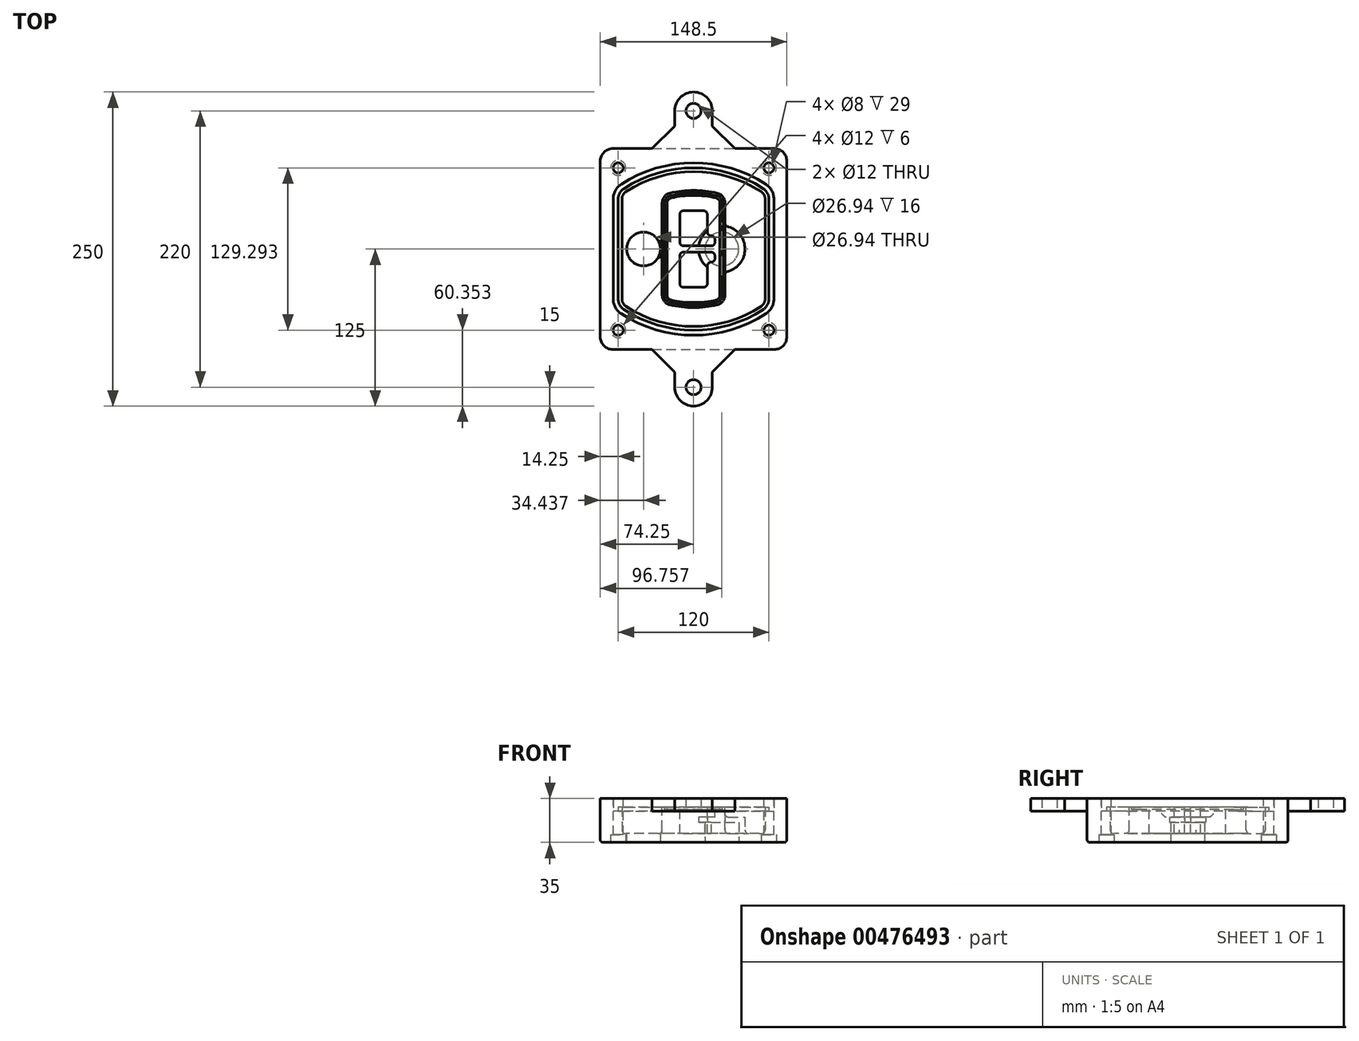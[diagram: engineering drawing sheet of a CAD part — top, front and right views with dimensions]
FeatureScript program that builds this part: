
annotation { "Feature Type Name" : "Feature", "Feature Type Description" : "" }
export const myFeature = defineFeature(function(context is Context, id is Id, definition is map)
    precondition{}
    {
        {
            var Q0;
            Q0=qCreatedBy(makeId("Top.planeOp"),FACE);
            var sketch = newSketch(context, id + "F0", { "sketchPlane" : qUnion([Q0])});
            skPoint(sketch, "E0.rect.middle", {"position": v(0, 0) * mm});
            skLineSegment(sketch, "E1.bottom", {"start": v(-64.25, -80) * mm, "end": v(64.25, -80) * mm});
            skLineSegment(sketch, "E1.top", {"start": v(-64.25, 80) * mm, "end": v(64.25, 80) * mm});
            skLineSegment(sketch, "E1.left", {"start": v(-74.25, -70) * mm, "end": v(-74.25, 70) * mm});
            skLineSegment(sketch, "E1.right", {"start": v(74.25, -70) * mm, "end": v(74.25, 70) * mm});
            skLineSegment(sketch, "E2", {"start": v(-74.25, 80) * mm, "end": v(74.25, -80) * mm, "construction": true});
            skLineSegment(sketch, "E3", {"start": v(74.25, 80) * mm, "end": v(-74.25, -80) * mm, "construction": true});
            skCircle(sketch, "E4", {"center": v(-60, 64.65) * mm, "radius": 4 * mm});
            skCircle(sketch, "E5", {"center": v(60, 64.65) * mm, "radius": 4 * mm});
            skCircle(sketch, "E6", {"center": v(60, -64.65) * mm, "radius": 4 * mm});
            skCircle(sketch, "E7", {"center": v(-60, -64.65) * mm, "radius": 4 * mm});
            skLineSegment(sketch, "E8", {"start": v(-60, 64.65) * mm, "end": v(60, 64.65) * mm, "construction": true});
            skLineSegment(sketch, "E9", {"start": v(60, 64.65) * mm, "end": v(60, -64.65) * mm, "construction": true});
            skLineSegment(sketch, "E10", {"start": v(60, -64.65) * mm, "end": v(-60, -64.65) * mm, "construction": true});
            skLineSegment(sketch, "E11", {"start": v(-60, -64.65) * mm, "end": v(-60, 64.65) * mm, "construction": true});
            skLineSegment(sketch, "E12", {"start": v(-60, 39.77) * mm, "end": v(-60, -39.77) * mm});
            skLineSegment(sketch, "E13", {"start": v(60, 39.77) * mm, "end": v(60, -39.77) * mm});
            skArc(sketch, "E14", {"start": v(55.47, 48.14) * mm, "mid": v(0, 64.65) * mm, "end": v(-55.47, 48.14) * mm});
            skArc(sketch, "E15", {"start": v(-55.47, -48.14) * mm, "mid": v(0, -64.65) * mm, "end": v(55.47, -48.14) * mm});
            skLineSegment(sketch, "E16", {"start": v(-60, 0) * mm, "end": v(60, 0) * mm, "construction": true});
            skPoint(sketch, "E17.visualSharp", {"position": v(-60, -45) * mm});
            skArc(sketch, "E17.filletArc", {"start": v(-60, -39.77) * mm, "mid": v(-58.8, -44.53) * mm, "end": v(-55.47, -48.14) * mm});
            skPoint(sketch, "E18.visualSharp", {"position": v(-60, 45) * mm});
            skArc(sketch, "E18.filletArc", {"start": v(-55.47, 48.14) * mm, "mid": v(-58.8, 44.53) * mm, "end": v(-60, 39.77) * mm});
            skPoint(sketch, "E19.visualSharp", {"position": v(60, 45) * mm});
            skArc(sketch, "E19.filletArc", {"start": v(60, 39.77) * mm, "mid": v(58.8, 44.53) * mm, "end": v(55.47, 48.14) * mm});
            skPoint(sketch, "E20.visualSharp", {"position": v(60, -45) * mm});
            skArc(sketch, "E20.filletArc", {"start": v(55.47, -48.14) * mm, "mid": v(58.8, -44.53) * mm, "end": v(60, -39.77) * mm});
            skPoint(sketch, "E21.visualSharp", {"position": v(-74.25, 80) * mm});
            skArc(sketch, "E21.filletArc", {"start": v(-64.25, 80) * mm, "mid": v(-71.32, 77.07) * mm, "end": v(-74.25, 70) * mm});
            skPoint(sketch, "E22.visualSharp", {"position": v(74.25, 80) * mm});
            skArc(sketch, "E22.filletArc", {"start": v(74.25, 70) * mm, "mid": v(71.32, 77.07) * mm, "end": v(64.25, 80) * mm});
            skPoint(sketch, "E23.visualSharp", {"position": v(74.25, -80) * mm});
            skArc(sketch, "E23.filletArc", {"start": v(64.25, -80) * mm, "mid": v(71.32, -77.07) * mm, "end": v(74.25, -70) * mm});
            skPoint(sketch, "E24.visualSharp", {"position": v(-74.25, -80) * mm});
            skArc(sketch, "E24.filletArc", {"start": v(-74.25, -70) * mm, "mid": v(-71.32, -77.07) * mm, "end": v(-64.25, -80) * mm});
            skArc(sketch, "E25.0", {"start": v(57, 39.77) * mm, "mid": v(56.16, 43.1) * mm, "end": v(53.83, 45.63) * mm});
            skLineSegment(sketch, "E25.1", {"start": v(57, 39.77) * mm, "end": v(57, -39.77) * mm});
            skArc(sketch, "E25.2", {"start": v(53.83, -45.63) * mm, "mid": v(56.16, -43.1) * mm, "end": v(57, -39.77) * mm});
            skArc(sketch, "E25.3", {"start": v(-53.83, -45.63) * mm, "mid": v(0, -61.65) * mm, "end": v(53.83, -45.63) * mm});
            skArc(sketch, "E25.4", {"start": v(-57, -39.77) * mm, "mid": v(-56.16, -43.1) * mm, "end": v(-53.83, -45.63) * mm});
            skArc(sketch, "E25.5", {"start": v(53.83, 45.63) * mm, "mid": v(0, 61.65) * mm, "end": v(-53.83, 45.63) * mm});
            skLineSegment(sketch, "E25.6", {"start": v(-57, 39.77) * mm, "end": v(-57, -39.77) * mm});
            skArc(sketch, "E25.7", {"start": v(-53.83, 45.63) * mm, "mid": v(-56.16, 43.1) * mm, "end": v(-57, 39.77) * mm});
            skArc(sketch, "E26.0", {"start": v(-57.66, 51.49) * mm, "mid": v(-62.31, 46.43) * mm, "end": v(-64, 39.77) * mm});
            skArc(sketch, "E26.1", {"start": v(57.66, 51.49) * mm, "mid": v(0, 68.65) * mm, "end": v(-57.66, 51.49) * mm});
            skArc(sketch, "E26.2", {"start": v(64, 39.77) * mm, "mid": v(62.31, 46.43) * mm, "end": v(57.66, 51.49) * mm});
            skLineSegment(sketch, "E26.3", {"start": v(64, 39.77) * mm, "end": v(64, -39.77) * mm});
            skArc(sketch, "E26.4", {"start": v(57.66, -51.49) * mm, "mid": v(62.31, -46.43) * mm, "end": v(64, -39.77) * mm});
            skLineSegment(sketch, "E26.5", {"start": v(-64, 39.77) * mm, "end": v(-64, -39.77) * mm});
            skArc(sketch, "E26.6", {"start": v(-57.66, -51.49) * mm, "mid": v(0, -68.65) * mm, "end": v(57.66, -51.49) * mm});
            skArc(sketch, "E26.7", {"start": v(-64, -39.77) * mm, "mid": v(-62.31, -46.43) * mm, "end": v(-57.66, -51.49) * mm});
            skPoint(sketch, "E27.startSnap0", {"position": v(0, 68.65) * mm});
            skPoint(sketch, "E27.endSnap0", {"position": v(0, 64.65) * mm});
            skLineSegment(sketch, "E28", {"start": v(0, 110) * mm, "end": v(0, 80) * mm, "construction": true});
            skCircle(sketch, "E29", {"center": v(0, 110) * mm, "radius": 6 * mm});
            skArc(sketch, "E30", {"start": v(15, 110) * mm, "mid": v(0, 125) * mm, "end": v(-15, 110) * mm});
            skLineSegment(sketch, "E31", {"start": v(-15, 110) * mm, "end": v(-15, 98) * mm});
            skLineSegment(sketch, "E32", {"start": v(-15, 98) * mm, "end": v(-33, 80) * mm});
            skLineSegment(sketch, "E33", {"start": v(15, 110) * mm, "end": v(15, 98) * mm});
            skLineSegment(sketch, "E34", {"start": v(15, 98) * mm, "end": v(33, 80) * mm});
            skLineSegment(sketch, "E35.MirrorCS", {"start": v(15, -110) * mm, "end": v(15, -98) * mm});
            skLineSegment(sketch, "E36.MirrorCS", {"start": v(-15, -110) * mm, "end": v(-15, -98) * mm});
            skLineSegment(sketch, "E37.MirrorCS", {"start": v(0, -110) * mm, "end": v(0, -80) * mm, "construction": true});
            skLineSegment(sketch, "E38.MirrorCS", {"start": v(-15, -98) * mm, "end": v(-33, -80) * mm});
            skPoint(sketch, "E39.MirrorP", {"position": v(0, -68.65) * mm});
            skArc(sketch, "E40.MirrorCS", {"start": v(15, -110) * mm, "mid": v(0, -125) * mm, "end": v(-15, -110) * mm});
            skLineSegment(sketch, "E41.MirrorCS", {"start": v(15, -98) * mm, "end": v(33, -80) * mm});
            skCircle(sketch, "E42.MirrorC", {"center": v(0, -110) * mm, "radius": 6 * mm});
            skSolve(sketch);
        }
        {
            var Q0;
            Q0=makeQuery(id+"F0.imprint","IMPRINT",FACE,{"disambiguationData":[TD([[makeQuery(id+"F0.imprint","IMPRINT",EDGE,{"derivedFrom":sQuery(id+"F0.wireOp",EDGE,"E1.bottom")}),1.0]])]});
            var Q1;
            Q1=makeQuery(id+"F0.imprint","IMPRINT",FACE,{"disambiguationData":[TD([[makeQuery(id+"F0.imprint","IMPRINT",EDGE,{"derivedFrom":sQuery(id+"F0.wireOp",EDGE,"E12")}),1.0]])]});
            var Q2;
            Q2=makeQuery(id+"F0.imprint","IMPRINT",FACE,{"disambiguationData":[TD([[makeQuery(id+"F0.imprint","IMPRINT",EDGE,{"derivedFrom":sQuery(id+"F0.wireOp",EDGE,"E25.0")}),1.0]])]});
            var Q3;
            Q3=makeQuery(id+"F0.imprint","IMPRINT",FACE,{"disambiguationData":[TD([[makeQuery(id+"F0.imprint","IMPRINT",EDGE,{"derivedFrom":sQuery(id+"F0.wireOp",EDGE,"E12")}),-1.0]])]});
            extrude(context, id + "F1", {"entities" : qUnion([Q0, Q1, Q2, Q3]), "oppositeDirection" : true, "depth" : 25 * mm});
        }
        {
            var Q0;
            Q0=makeQuery(id+"F0.imprint","IMPRINT",FACE,{"disambiguationData":[TD([[makeQuery(id+"F0.imprint","IMPRINT",EDGE,{"derivedFrom":sQuery(id+"F0.wireOp",EDGE,"E12")}),1.0]])]});
            extrude(context, id + "F2", {"entities" : qUnion([Q0]), "operationType" : NewBodyOperationType.ADD, "depth" : 3 * mm});
        }
        {
            var Q0;
            Q0=makeQuery(id+"F0.imprint","IMPRINT",FACE,{"disambiguationData":[TD([[makeQuery(id+"F0.imprint","IMPRINT",EDGE,{"derivedFrom":sQuery(id+"F0.wireOp",EDGE,"E25.0")}),1.0]])]});
            extrude(context, id + "F3", {"entities" : qUnion([Q0]), "operationType" : NewBodyOperationType.REMOVE, "oppositeDirection" : true, "depth" : 18 * mm});
        }
        {
            var Q0;
            Q0=makeQuery(id+"F2.opExtrude","CAP_FACE",FACE,{"disambiguationData":[OSD([sQuery(id+"F0.wireOp",EDGE,"E12"),sQuery(id+"F0.wireOp",EDGE,"E13"),sQuery(id+"F0.wireOp",EDGE,"E14"),sQuery(id+"F0.wireOp",EDGE,"E15"),sQuery(id+"F0.wireOp",EDGE,"E17.filletArc"),sQuery(id+"F0.wireOp",EDGE,"E18.filletArc"),sQuery(id+"F0.wireOp",EDGE,"E19.filletArc"),sQuery(id+"F0.wireOp",EDGE,"E20.filletArc"),sQuery(id+"F0.wireOp",EDGE,"E25.0"),sQuery(id+"F0.wireOp",EDGE,"E25.1"),sQuery(id+"F0.wireOp",EDGE,"E25.2"),sQuery(id+"F0.wireOp",EDGE,"E25.3"),sQuery(id+"F0.wireOp",EDGE,"E25.4"),sQuery(id+"F0.wireOp",EDGE,"E25.5"),sQuery(id+"F0.wireOp",EDGE,"E25.6"),sQuery(id+"F0.wireOp",EDGE,"E25.7")])],"isStart":false});
            var sketch = newSketch(context, id + "F4", { "sketchPlane" : qUnion([Q0])});
            skArc(sketch, "E43.0", {"start": v(-18.8, -44.5) * mm, "mid": v(0, -46.65) * mm, "end": v(18.8, -44.5) * mm});
            skArc(sketch, "E44.0", {"start": v(18.8, 44.5) * mm, "mid": v(0, 46.65) * mm, "end": v(-18.8, 44.5) * mm});
            skLineSegment(sketch, "E45", {"start": v(-25, 36.7) * mm, "end": v(-25, -36.7) * mm});
            skLineSegment(sketch, "E46", {"start": v(25, 36.7) * mm, "end": v(25, -36.7) * mm});
            skLineSegment(sketch, "E47", {"start": v(-25, 42.81) * mm, "end": v(25, 42.81) * mm, "construction": true});
            skLineSegment(sketch, "E48", {"start": v(-25, -42.81) * mm, "end": v(25, -42.81) * mm, "construction": true});
            skPoint(sketch, "E49.visualSharp", {"position": v(-25, 42.81) * mm});
            skArc(sketch, "E49.filletArc", {"start": v(-18.8, 44.5) * mm, "mid": v(-23.26, 41.69) * mm, "end": v(-25, 36.7) * mm});
            skPoint(sketch, "E50.visualSharp", {"position": v(25, 42.81) * mm});
            skArc(sketch, "E50.filletArc", {"start": v(25, 36.7) * mm, "mid": v(23.26, 41.69) * mm, "end": v(18.8, 44.5) * mm});
            skPoint(sketch, "E51.visualSharp", {"position": v(25, -42.81) * mm});
            skArc(sketch, "E51.filletArc", {"start": v(18.8, -44.5) * mm, "mid": v(23.26, -41.69) * mm, "end": v(25, -36.7) * mm});
            skPoint(sketch, "E52.visualSharp", {"position": v(-25, -42.81) * mm});
            skArc(sketch, "E52.filletArc", {"start": v(-25, -36.7) * mm, "mid": v(-23.26, -41.69) * mm, "end": v(-18.8, -44.5) * mm});
            skArc(sketch, "E53.0", {"start": v(53.83, 45.63) * mm, "mid": v(0, 61.65) * mm, "end": v(-53.83, 45.63) * mm});
            skArc(sketch, "E53.1", {"start": v(-53.83, 45.63) * mm, "mid": v(-56.16, 43.1) * mm, "end": v(-57, 39.77) * mm});
            skLineSegment(sketch, "E53.2", {"start": v(-57, 39.77) * mm, "end": v(-57, -39.77) * mm});
            skArc(sketch, "E53.3", {"start": v(-57, -39.77) * mm, "mid": v(-56.16, -43.1) * mm, "end": v(-53.83, -45.63) * mm});
            skArc(sketch, "E53.4", {"start": v(-53.83, -45.63) * mm, "mid": v(0, -61.65) * mm, "end": v(53.83, -45.63) * mm});
            skArc(sketch, "E53.5", {"start": v(53.83, -45.63) * mm, "mid": v(56.16, -43.1) * mm, "end": v(57, -39.77) * mm});
            skLineSegment(sketch, "E53.6", {"start": v(57, 39.77) * mm, "end": v(57, -39.77) * mm});
            skArc(sketch, "E53.7", {"start": v(57, 39.77) * mm, "mid": v(56.16, 43.1) * mm, "end": v(53.83, 45.63) * mm});
            skLineSegment(sketch, "E54.0", {"start": v(23, 36.7) * mm, "end": v(23, -36.7) * mm});
            skArc(sketch, "E54.1", {"start": v(18.35, -42.55) * mm, "mid": v(21.7, -40.44) * mm, "end": v(23, -36.7) * mm});
            skArc(sketch, "E54.2", {"start": v(-18.35, -42.55) * mm, "mid": v(0, -44.65) * mm, "end": v(18.35, -42.55) * mm});
            skArc(sketch, "E54.3", {"start": v(-23, -36.7) * mm, "mid": v(-21.7, -40.44) * mm, "end": v(-18.35, -42.55) * mm});
            skLineSegment(sketch, "E54.4", {"start": v(-23, 36.7) * mm, "end": v(-23, -36.7) * mm});
            skArc(sketch, "E54.5", {"start": v(23, 36.7) * mm, "mid": v(21.7, 40.44) * mm, "end": v(18.35, 42.55) * mm});
            skArc(sketch, "E54.6", {"start": v(-18.35, 42.55) * mm, "mid": v(-21.7, 40.44) * mm, "end": v(-23, 36.7) * mm});
            skArc(sketch, "E54.7", {"start": v(18.35, 42.55) * mm, "mid": v(0, 44.65) * mm, "end": v(-18.35, 42.55) * mm});
            skArc(sketch, "E55.0", {"start": v(21, 36.7) * mm, "mid": v(20.13, 39.2) * mm, "end": v(17.9, 40.6) * mm});
            skLineSegment(sketch, "E55.1", {"start": v(21, 36.7) * mm, "end": v(21, -36.7) * mm});
            skArc(sketch, "E55.2", {"start": v(17.9, -40.6) * mm, "mid": v(20.13, -39.2) * mm, "end": v(21, -36.7) * mm});
            skArc(sketch, "E55.3", {"start": v(-17.9, -40.6) * mm, "mid": v(0, -42.65) * mm, "end": v(17.9, -40.6) * mm});
            skArc(sketch, "E55.4", {"start": v(-21, -36.7) * mm, "mid": v(-20.13, -39.2) * mm, "end": v(-17.9, -40.6) * mm});
            skArc(sketch, "E55.5", {"start": v(17.9, 40.6) * mm, "mid": v(0, 42.65) * mm, "end": v(-17.9, 40.6) * mm});
            skLineSegment(sketch, "E55.6", {"start": v(-21, 36.7) * mm, "end": v(-21, -36.7) * mm});
            skArc(sketch, "E55.7", {"start": v(-17.9, 40.6) * mm, "mid": v(-20.13, 39.2) * mm, "end": v(-21, 36.7) * mm});
            skLineSegment(sketch, "E56", {"start": v(-25, 0) * mm, "end": v(25, 0) * mm, "construction": true});
            skLineSegment(sketch, "E57", {"start": v(-11, 5.5) * mm, "end": v(-11, 27.5) * mm});
            skLineSegment(sketch, "E58", {"start": v(-8, 30.5) * mm, "end": v(8, 30.5) * mm});
            skLineSegment(sketch, "E59", {"start": v(11, 27.5) * mm, "end": v(11, 13.5) * mm});
            skLineSegment(sketch, "E60", {"start": v(14, 10.5) * mm, "end": v(14, 10.5) * mm});
            skLineSegment(sketch, "E61", {"start": v(17, 7.5) * mm, "end": v(17, 5.5) * mm});
            skLineSegment(sketch, "E62", {"start": v(14, 2.5) * mm, "end": v(-8, 2.5) * mm});
            skPoint(sketch, "E63.visualSharp", {"position": v(-11, 30.5) * mm});
            skArc(sketch, "E63.filletArc", {"start": v(-8, 30.5) * mm, "mid": v(-10.12, 29.62) * mm, "end": v(-11, 27.5) * mm});
            skPoint(sketch, "E64.visualSharp", {"position": v(11, 30.5) * mm});
            skArc(sketch, "E64.filletArc", {"start": v(11, 27.5) * mm, "mid": v(10.12, 29.62) * mm, "end": v(8, 30.5) * mm});
            skPoint(sketch, "E65.visualSharp", {"position": v(11, 10.5) * mm});
            skArc(sketch, "E65.filletArc", {"start": v(11, 13.5) * mm, "mid": v(11.88, 11.38) * mm, "end": v(14, 10.5) * mm});
            skPoint(sketch, "E66.visualSharp", {"position": v(17, 10.5) * mm});
            skArc(sketch, "E66.filletArc", {"start": v(17, 7.5) * mm, "mid": v(16.12, 9.62) * mm, "end": v(14, 10.5) * mm});
            skPoint(sketch, "E67.visualSharp", {"position": v(17, 2.5) * mm});
            skArc(sketch, "E67.filletArc", {"start": v(14, 2.5) * mm, "mid": v(16.12, 3.38) * mm, "end": v(17, 5.5) * mm});
            skPoint(sketch, "E68.visualSharp", {"position": v(-11, 2.5) * mm});
            skArc(sketch, "E68.filletArc", {"start": v(-11, 5.5) * mm, "mid": v(-10.12, 3.38) * mm, "end": v(-8, 2.5) * mm});
            skLineSegment(sketch, "E69.0.MirrorCS", {"start": v(14, -2.5) * mm, "end": v(-8, -2.5) * mm});
            skArc(sketch, "E70.0.MirrorCS", {"start": v(-11, -5.5) * mm, "mid": v(-10.12, -3.38) * mm, "end": v(-8, -2.5) * mm});
            skLineSegment(sketch, "E71.0.MirrorCS", {"start": v(-11, -5.5) * mm, "end": v(-11, -27.5) * mm});
            skArc(sketch, "E72.0.MirrorCS", {"start": v(-8, -30.5) * mm, "mid": v(-10.12, -29.62) * mm, "end": v(-11, -27.5) * mm});
            skLineSegment(sketch, "E73.0.MirrorCS", {"start": v(-8, -30.5) * mm, "end": v(8, -30.5) * mm});
            skArc(sketch, "E74.0.MirrorCS", {"start": v(11, -27.5) * mm, "mid": v(10.12, -29.62) * mm, "end": v(8, -30.5) * mm});
            skLineSegment(sketch, "E75.0.MirrorCS", {"start": v(11, -27.5) * mm, "end": v(11, -13.5) * mm});
            skArc(sketch, "E76.0.MirrorCS", {"start": v(11, -13.5) * mm, "mid": v(11.88, -11.38) * mm, "end": v(14, -10.5) * mm});
            skArc(sketch, "E77.0.MirrorCS", {"start": v(17, -7.5) * mm, "mid": v(16.12, -9.62) * mm, "end": v(14, -10.5) * mm});
            skLineSegment(sketch, "E78.0.MirrorCS", {"start": v(17, -7.5) * mm, "end": v(17, -5.5) * mm});
            skArc(sketch, "E79.0.MirrorCS", {"start": v(14, -2.5) * mm, "mid": v(16.12, -3.38) * mm, "end": v(17, -5.5) * mm});
            skSolve(sketch);
        }
        {
            var Q0;
            Q0=makeQuery(id+"F4.imprint","IMPRINT",FACE,{"disambiguationData":[TD([[makeQuery(id+"F4.imprint","IMPRINT",EDGE,{"derivedFrom":sQuery(id+"F4.wireOp",EDGE,"E43.0")}),1.0]])]});
            var Q1;
            Q1=makeQuery(id+"F4.imprint","IMPRINT",FACE,{"disambiguationData":[TD([[makeQuery(id+"F4.imprint","IMPRINT",EDGE,{"derivedFrom":sQuery(id+"F4.wireOp",EDGE,"E54.0")}),-1.0]])]});
            var Q2;
            Q2=makeQuery(id+"F4.imprint","IMPRINT",FACE,{"disambiguationData":[TD([[makeQuery(id+"F4.imprint","IMPRINT",EDGE,{"derivedFrom":sQuery(id+"F4.wireOp",EDGE,"E55.0")}),1.0]])]});
            extrude(context, id + "F5", {"entities" : qUnion([Q0, Q1, Q2]), "operationType" : NewBodyOperationType.ADD, "endBound" : BoundingType.UP_TO_NEXT, "oppositeDirection" : true, "depth" : 25 * mm});
        }
        {
            var Q0;
            Q0=makeQuery(id+"F4.imprint","IMPRINT",FACE,{"disambiguationData":[TD([[makeQuery(id+"F4.imprint","IMPRINT",EDGE,{"derivedFrom":sQuery(id+"F4.wireOp",EDGE,"E54.0")}),-1.0]])]});
            extrude(context, id + "F6", {"entities" : qUnion([Q0]), "operationType" : NewBodyOperationType.REMOVE, "oppositeDirection" : true, "depth" : 2 * mm});
        }
        {
            var Q0;
            Q0=makeQuery(id+"F1.opExtrude","CAP_FACE",FACE,{"disambiguationData":[OSD([sQuery(id+"F0.wireOp",EDGE,"E1.bottom"),sQuery(id+"F0.wireOp",EDGE,"E1.top"),sQuery(id+"F0.wireOp",EDGE,"E1.left"),sQuery(id+"F0.wireOp",EDGE,"E1.right"),sQuery(id+"F0.wireOp",EDGE,"E4"),sQuery(id+"F0.wireOp",EDGE,"E5"),sQuery(id+"F0.wireOp",EDGE,"E6"),sQuery(id+"F0.wireOp",EDGE,"E7"),sQuery(id+"F0.wireOp",EDGE,"E21.filletArc"),sQuery(id+"F0.wireOp",EDGE,"E22.filletArc"),sQuery(id+"F0.wireOp",EDGE,"E23.filletArc"),sQuery(id+"F0.wireOp",EDGE,"E24.filletArc")])],"isStart":false});
            var sketch = newSketch(context, id + "F7", { "sketchPlane" : qUnion([Q0])});
            skCircle(sketch, "E80", {"center": v(22.5, 0) * mm, "radius": 13.47 * mm});
            skCircle(sketch, "E81", {"center": v(-39.81, 0) * mm, "radius": 13.47 * mm});
            skLineSegment(sketch, "E82", {"start": v(74.25, 0) * mm, "end": v(-74.25, 0) * mm});
            skCircle(sketch, "E83", {"center": v(22.5, 0) * mm, "radius": 18.47 * mm});
            skCircle(sketch, "E84", {"center": v(60, -64.65) * mm, "radius": 6 * mm});
            skCircle(sketch, "E85", {"center": v(-60, -64.65) * mm, "radius": 6 * mm});
            skCircle(sketch, "E86", {"center": v(-60, 64.65) * mm, "radius": 6 * mm});
            skCircle(sketch, "E87", {"center": v(60, 64.65) * mm, "radius": 6 * mm});
            skSolve(sketch);
        }
        {
            var Q0;
            {var subQ1=sQuery(id+"F7.wireOp",EDGE,"E82");var subQ4=sQuery(id+"F7.wireOp",EDGE,"E80");var subQ6=makeQuery(id+"F7.imprint","INTERSECT",VERTEX,{"disambiguationData":[OD(0.0)],"derivedFrom":[subQ4,subQ1]});Q0=makeQuery(id+"F7.imprint","IMPRINT",FACE,{"disambiguationData":[TD([[makeQuery(id+"F7.imprint","IMPRINT",EDGE,{"disambiguationData":[TD([[subQ6,-1.0]])],"derivedFrom":subQ4}),-1.0]])]});}
            var Q1;
            {var subQ0=sQuery(id+"F7.wireOp",EDGE,"E82");var subQ1=sQuery(id+"F7.wireOp",EDGE,"E80");var subQ3=makeQuery(id+"F7.imprint","INTERSECT",VERTEX,{"disambiguationData":[OD(0.0)],"derivedFrom":[subQ1,subQ0]});Q1=makeQuery(id+"F7.imprint","IMPRINT",FACE,{"disambiguationData":[TD([[makeQuery(id+"F7.imprint","IMPRINT",EDGE,{"disambiguationData":[TD([[subQ3,-1.0]])],"derivedFrom":subQ1}),1.0]])]});}
            var Q2;
            {var subQ0=sQuery(id+"F7.wireOp",EDGE,"E82");var subQ1=sQuery(id+"F7.wireOp",EDGE,"E80");var subQ3=makeQuery(id+"F7.imprint","INTERSECT",VERTEX,{"disambiguationData":[OD(0.0)],"derivedFrom":[subQ1,subQ0]});Q2=makeQuery(id+"F7.imprint","IMPRINT",FACE,{"disambiguationData":[TD([[makeQuery(id+"F7.imprint","IMPRINT",EDGE,{"disambiguationData":[TD([[subQ3,1.0]])],"derivedFrom":subQ1}),1.0]])]});}
            var Q3;
            {var subQ1=sQuery(id+"F7.wireOp",EDGE,"E82");var subQ4=sQuery(id+"F7.wireOp",EDGE,"E80");var subQ6=makeQuery(id+"F7.imprint","INTERSECT",VERTEX,{"disambiguationData":[OD(0.0)],"derivedFrom":[subQ4,subQ1]});Q3=makeQuery(id+"F7.imprint","IMPRINT",FACE,{"disambiguationData":[TD([[makeQuery(id+"F7.imprint","IMPRINT",EDGE,{"disambiguationData":[TD([[subQ6,1.0]])],"derivedFrom":subQ4}),-1.0]])]});}
            extrude(context, id + "F8", {"entities" : qUnion([Q0, Q1, Q2, Q3]), "operationType" : NewBodyOperationType.ADD, "oppositeDirection" : true, "depth" : 20 * mm});
        }
        {
            var Q0;
            {var subQ0=sQuery(id+"F7.wireOp",EDGE,"E82");var subQ1=sQuery(id+"F7.wireOp",EDGE,"E80");var subQ3=makeQuery(id+"F7.imprint","INTERSECT",VERTEX,{"disambiguationData":[OD(0.0)],"derivedFrom":[subQ1,subQ0]});Q0=makeQuery(id+"F7.imprint","IMPRINT",FACE,{"disambiguationData":[TD([[makeQuery(id+"F7.imprint","IMPRINT",EDGE,{"disambiguationData":[TD([[subQ3,-1.0]])],"derivedFrom":subQ1}),1.0]])]});}
            var Q1;
            {var subQ0=sQuery(id+"F7.wireOp",EDGE,"E82");var subQ1=sQuery(id+"F7.wireOp",EDGE,"E80");var subQ3=makeQuery(id+"F7.imprint","INTERSECT",VERTEX,{"disambiguationData":[OD(0.0)],"derivedFrom":[subQ1,subQ0]});Q1=makeQuery(id+"F7.imprint","IMPRINT",FACE,{"disambiguationData":[TD([[makeQuery(id+"F7.imprint","IMPRINT",EDGE,{"disambiguationData":[TD([[subQ3,1.0]])],"derivedFrom":subQ1}),1.0]])]});}
            extrude(context, id + "F9", {"entities" : qUnion([Q0, Q1]), "operationType" : NewBodyOperationType.REMOVE, "oppositeDirection" : true, "depth" : 16 * mm});
        }
        {
            var Q0;
            {var subQ0=sQuery(id+"F7.wireOp",EDGE,"E82");var subQ1=sQuery(id+"F7.wireOp",EDGE,"E81");var subQ3=makeQuery(id+"F7.imprint","INTERSECT",VERTEX,{"disambiguationData":[OD(0.0)],"derivedFrom":[subQ1,subQ0]});Q0=makeQuery(id+"F7.imprint","IMPRINT",FACE,{"disambiguationData":[TD([[makeQuery(id+"F7.imprint","IMPRINT",EDGE,{"disambiguationData":[TD([[subQ3,-1.0]])],"derivedFrom":subQ1}),1.0]])]});}
            var Q1;
            {var subQ0=sQuery(id+"F7.wireOp",EDGE,"E82");var subQ1=sQuery(id+"F7.wireOp",EDGE,"E81");var subQ3=makeQuery(id+"F7.imprint","INTERSECT",VERTEX,{"disambiguationData":[OD(0.0)],"derivedFrom":[subQ1,subQ0]});Q1=makeQuery(id+"F7.imprint","IMPRINT",FACE,{"disambiguationData":[TD([[makeQuery(id+"F7.imprint","IMPRINT",EDGE,{"disambiguationData":[TD([[subQ3,1.0]])],"derivedFrom":subQ1}),1.0]])]});}
            extrude(context, id + "F10", {"entities" : qUnion([Q0, Q1]), "operationType" : NewBodyOperationType.REMOVE, "oppositeDirection" : true, "depth" : 25 * mm});
        }
        {
            var Q0;
            Q0=makeQuery(id+"F7.imprint","IMPRINT",FACE,{"disambiguationData":[TD([[makeQuery(id+"F7.imprint","IMPRINT",EDGE,{"derivedFrom":sQuery(id+"F7.wireOp",EDGE,"E84")}),1.0]])]});
            var Q1;
            Q1=makeQuery(id+"F7.imprint","IMPRINT",FACE,{"disambiguationData":[TD([[makeQuery(id+"F7.imprint","IMPRINT",EDGE,{"derivedFrom":makeQuery(id+"F1.opExtrude","CAP_EDGE",EDGE,{"disambiguationData":[OSD([sQuery(id+"F0.wireOp",EDGE,"E5")])],"isStart":false})}),-1.0]])]});
            var Q2;
            Q2=makeQuery(id+"F7.imprint","IMPRINT",FACE,{"disambiguationData":[TD([[makeQuery(id+"F7.imprint","IMPRINT",EDGE,{"derivedFrom":sQuery(id+"F7.wireOp",EDGE,"E85")}),1.0]])]});
            var Q3;
            Q3=makeQuery(id+"F7.imprint","IMPRINT",FACE,{"disambiguationData":[TD([[makeQuery(id+"F7.imprint","IMPRINT",EDGE,{"derivedFrom":makeQuery(id+"F1.opExtrude","CAP_EDGE",EDGE,{"disambiguationData":[OSD([sQuery(id+"F0.wireOp",EDGE,"E4")])],"isStart":false})}),-1.0]])]});
            var Q4;
            Q4=makeQuery(id+"F7.imprint","IMPRINT",FACE,{"disambiguationData":[TD([[makeQuery(id+"F7.imprint","IMPRINT",EDGE,{"derivedFrom":sQuery(id+"F7.wireOp",EDGE,"E86")}),1.0]])]});
            var Q5;
            Q5=makeQuery(id+"F7.imprint","IMPRINT",FACE,{"disambiguationData":[TD([[makeQuery(id+"F7.imprint","IMPRINT",EDGE,{"derivedFrom":makeQuery(id+"F1.opExtrude","CAP_EDGE",EDGE,{"disambiguationData":[OSD([sQuery(id+"F0.wireOp",EDGE,"E7")])],"isStart":false})}),-1.0]])]});
            var Q6;
            Q6=makeQuery(id+"F7.imprint","IMPRINT",FACE,{"disambiguationData":[TD([[makeQuery(id+"F7.imprint","IMPRINT",EDGE,{"derivedFrom":sQuery(id+"F7.wireOp",EDGE,"E87")}),1.0]])]});
            var Q7;
            Q7=makeQuery(id+"F7.imprint","IMPRINT",FACE,{"disambiguationData":[TD([[makeQuery(id+"F7.imprint","IMPRINT",EDGE,{"derivedFrom":makeQuery(id+"F1.opExtrude","CAP_EDGE",EDGE,{"disambiguationData":[OSD([sQuery(id+"F0.wireOp",EDGE,"E6")])],"isStart":false})}),-1.0]])]});
            extrude(context, id + "F11", {"entities" : qUnion([Q0, Q1, Q2, Q3, Q4, Q5, Q6, Q7]), "operationType" : NewBodyOperationType.REMOVE, "oppositeDirection" : true, "depth" : 6 * mm});
        }
        {
            var Q0;
            Q0=makeQuery(id+"F9.boolean.opBoolean","COPY",FACE,{"derivedFrom":makeQuery(id+"F9.opExtrude","CAP_FACE",FACE,{"disambiguationData":[OSD([sQuery(id+"F7.wireOp",EDGE,"E80")])],"isStart":false})});
            var sketch = newSketch(context, id + "F12", { "sketchPlane" : qUnion([Q0])});
            skArc(sketch, "E88.0", {"start": v(11, 14.45) * mm, "mid": v(6.45, 9.13) * mm, "end": v(4.2, 2.5) * mm});
            skArc(sketch, "E88.1", {"start": v(4.2, -2.5) * mm, "mid": v(6.45, -9.13) * mm, "end": v(11, -14.45) * mm});
            skLineSegment(sketch, "E89", {"start": v(4.2, -2.5) * mm, "end": v(14, -2.5) * mm});
            skLineSegment(sketch, "E90.0", {"start": v(14, 2.5) * mm, "end": v(4.2, 2.5) * mm});
            skArc(sketch, "E90.1", {"start": v(14, 2.5) * mm, "mid": v(16.12, 3.38) * mm, "end": v(17, 5.5) * mm});
            skLineSegment(sketch, "E90.2", {"start": v(17, 7.5) * mm, "end": v(17, 5.5) * mm});
            skArc(sketch, "E90.3", {"start": v(17, 7.5) * mm, "mid": v(16.12, 9.62) * mm, "end": v(14, 10.5) * mm});
            skArc(sketch, "E90.4", {"start": v(11, 13.5) * mm, "mid": v(11.88, 11.38) * mm, "end": v(14, 10.5) * mm});
            skLineSegment(sketch, "E90.5", {"start": v(11, 14.45) * mm, "end": v(11, 13.5) * mm});
            skLineSegment(sketch, "E90.7", {"start": v(14, -2.5) * mm, "end": v(4.2, -2.5) * mm});
            skArc(sketch, "E90.8", {"start": v(14, -2.5) * mm, "mid": v(16.12, -3.38) * mm, "end": v(17, -5.5) * mm});
            skLineSegment(sketch, "E90.9", {"start": v(17, -7.5) * mm, "end": v(17, -5.5) * mm});
            skArc(sketch, "E90.10", {"start": v(17, -7.5) * mm, "mid": v(16.12, -9.62) * mm, "end": v(14, -10.5) * mm});
            skArc(sketch, "E90.11", {"start": v(11, -13.5) * mm, "mid": v(11.88, -11.38) * mm, "end": v(14, -10.5) * mm});
            skLineSegment(sketch, "E90.12", {"start": v(11, -14.45) * mm, "end": v(11, -13.5) * mm});
            skPoint(sketch, "E91.orphan", {"position": v(11, -27.5) * mm});
            skPoint(sketch, "E92.orphan", {"position": v(-8, -2.5) * mm});
            skPoint(sketch, "E93.orphan", {"position": v(-8, 2.5) * mm});
            skPoint(sketch, "E94.orphan", {"position": v(11, 27.5) * mm});
            skSolve(sketch);
        }
        {
            var Q0;
            {var subQ7=sQuery(id+"F12.wireOp",EDGE,"E88.0");var subQ14=sQuery(id+"F12.wireOp",EDGE,"E88.1");var subQ16=sQuery(id+"F12.wireOp",EDGE,"E90.1");var subQ18=sQuery(id+"F12.wireOp",EDGE,"E90.8");Q0=qUnion([makeQuery(id+"F12.imprint","IMPRINT",FACE,{"disambiguationData":[TD([[makeQuery(id+"F12.imprint","IMPRINT",EDGE,{"derivedFrom":subQ7}),1.0]])]}),makeQuery(id+"F12.imprint","IMPRINT",FACE,{"disambiguationData":[TD([[makeQuery(id+"F12.imprint","IMPRINT",EDGE,{"derivedFrom":subQ14}),1.0]])]}),makeQuery(id+"F12.imprint","IMPRINT",FACE,{"disambiguationData":[TD([[makeQuery(id+"F12.imprint","IMPRINT",EDGE,{"derivedFrom":subQ16}),1.0]])]}),makeQuery(id+"F12.imprint","IMPRINT",FACE,{"disambiguationData":[TD([[makeQuery(id+"F12.imprint","IMPRINT",EDGE,{"derivedFrom":subQ18}),-1.0]])]})]);}
            var Q1;
            Q1=makeQuery(id+"F5.boolean.opBoolean","SPLIT",FACE,{"disambiguationData":[TD([makeQuery(id+"F5.opExtrude","SWEPT_FACE",FACE,{"disambiguationData":[OSD([sQuery(id+"F4.wireOp",EDGE,"E57")])]})])],"derivedFrom":makeQuery(id+"F3.boolean.opBoolean","COPY",FACE,{"derivedFrom":makeQuery(id+"F3.opExtrude","CAP_FACE",FACE,{"disambiguationData":[OSD([sQuery(id+"F0.wireOp",EDGE,"E25.0"),sQuery(id+"F0.wireOp",EDGE,"E25.1"),sQuery(id+"F0.wireOp",EDGE,"E25.2"),sQuery(id+"F0.wireOp",EDGE,"E25.3"),sQuery(id+"F0.wireOp",EDGE,"E25.4"),sQuery(id+"F0.wireOp",EDGE,"E25.5"),sQuery(id+"F0.wireOp",EDGE,"E25.6"),sQuery(id+"F0.wireOp",EDGE,"E25.7")])],"isStart":false})})});
            extrude(context, id + "F13", {"entities" : qUnion([Q0]), "operationType" : NewBodyOperationType.REMOVE, "endBound" : BoundingType.UP_TO_SURFACE, "endBoundEntityFace" : qUnion([Q1]), "depth" : 25 * mm});
        }
        {
            var Q0;
            Q0=makeQuery(id+"F3.boolean.opBoolean","COPY",EDGE,{"derivedFrom":makeQuery(id+"F3.opExtrude","CAP_EDGE",EDGE,{"disambiguationData":[OSD([sQuery(id+"F0.wireOp",EDGE,"E25.6")])],"isStart":false})});
            var Q1;
            Q1=makeQuery(id+"F8.boolean.opBoolean","INTERSECT",EDGE,{"derivedFrom":[makeQuery(id+"F5.opExtrude","SWEPT_FACE",FACE,{"disambiguationData":[OSD([sQuery(id+"F4.wireOp",EDGE,"E46")])]}),makeQuery(id+"F8.opExtrude","CAP_FACE",FACE,{"disambiguationData":[OSD([sQuery(id+"F7.wireOp",EDGE,"E83")])],"isStart":false})]});
            var Q2;
            Q2=makeQuery(id+"F8.boolean.opBoolean","INTERSECT",EDGE,{"disambiguationData":[OD(1.0)],"derivedFrom":[makeQuery(id+"F5.opExtrude","SWEPT_FACE",FACE,{"disambiguationData":[OSD([sQuery(id+"F4.wireOp",EDGE,"E46")])]}),makeQuery(id+"F8.opExtrude","SWEPT_FACE",FACE,{"disambiguationData":[OSD([sQuery(id+"F7.wireOp",EDGE,"E83")])]})]});
            var Q3;
            {var subQ0=sQuery(id+"F4.wireOp",EDGE,"E46");Q3=makeQuery(id+"F8.boolean.opBoolean","SPLIT",EDGE,{"disambiguationData":[TD([makeQuery(id+"F5.opExtrude","SWEPT_FACE",FACE,{"disambiguationData":[OSD([sQuery(id+"F4.wireOp",EDGE,"E51.filletArc")])]})])],"derivedFrom":makeQuery(id+"F5.opExtrude","CAP_EDGE",EDGE,{"disambiguationData":[OSD([subQ0])],"isStart":false})});}
            var Q4;
            {var subQ0=sQuery(id+"F0.wireOp",EDGE,"E25.7");var subQ1=sQuery(id+"F0.wireOp",EDGE,"E25.1");var subQ2=sQuery(id+"F0.wireOp",EDGE,"E25.6");var subQ3=sQuery(id+"F0.wireOp",EDGE,"E25.5");var subQ4=sQuery(id+"F0.wireOp",EDGE,"E25.4");var subQ5=sQuery(id+"F0.wireOp",EDGE,"E25.0");var subQ6=sQuery(id+"F0.wireOp",EDGE,"E25.2");var subQ7=sQuery(id+"F0.wireOp",EDGE,"E25.3");Q4=makeQuery(id+"F8.boolean.opBoolean","INTERSECT",EDGE,{"derivedFrom":[makeQuery(id+"F5.boolean.opBoolean","SPLIT",FACE,{"disambiguationData":[TD([makeQuery(id+"F2.opExtrude","SWEPT_FACE",FACE,{"disambiguationData":[OSD([subQ5])]})])],"derivedFrom":makeQuery(id+"F3.boolean.opBoolean","COPY",FACE,{"derivedFrom":makeQuery(id+"F3.opExtrude","CAP_FACE",FACE,{"disambiguationData":[OSD([subQ5,subQ1,subQ6,subQ7,subQ4,subQ3,subQ2,subQ0])],"isStart":false})})}),makeQuery(id+"F8.opExtrude","SWEPT_FACE",FACE,{"disambiguationData":[OSD([sQuery(id+"F7.wireOp",EDGE,"E83")])]})]});}
            var Q5;
            Q5=makeQuery(id+"F8.boolean.opBoolean","INTERSECT",EDGE,{"disambiguationData":[OD(0.0)],"derivedFrom":[makeQuery(id+"F5.opExtrude","SWEPT_FACE",FACE,{"disambiguationData":[OSD([sQuery(id+"F4.wireOp",EDGE,"E46")])]}),makeQuery(id+"F8.opExtrude","SWEPT_FACE",FACE,{"disambiguationData":[OSD([sQuery(id+"F7.wireOp",EDGE,"E83")])]})]});
            fillet(context, id + "F14", {"entities" : qUnion([Q0, Q1, Q2, Q3, Q4, Q5]), "radius" : 3 * mm, "tangentPropagation" : true, "allowEdgeOverflow" : false});
        }
        {
            var Q0;
            Q0=makeQuery(id+"F1.opExtrude","CAP_EDGE",EDGE,{"disambiguationData":[OSD([sQuery(id+"F0.wireOp",EDGE,"E1.bottom")])],"isStart":false});
            fillet(context, id + "F15", {"entities" : qUnion([Q0]), "radius" : 2 * mm, "tangentPropagation" : true, "allowEdgeOverflow" : false});
        }
        {
            var Q0;
            Q0 = qSketchRegion(id + "F0", true);
            extrude(context, id + "F16", {"entities" : qUnion([Q0]), "operationType" : NewBodyOperationType.ADD, "depth" : 10 * mm});
        }
    });
